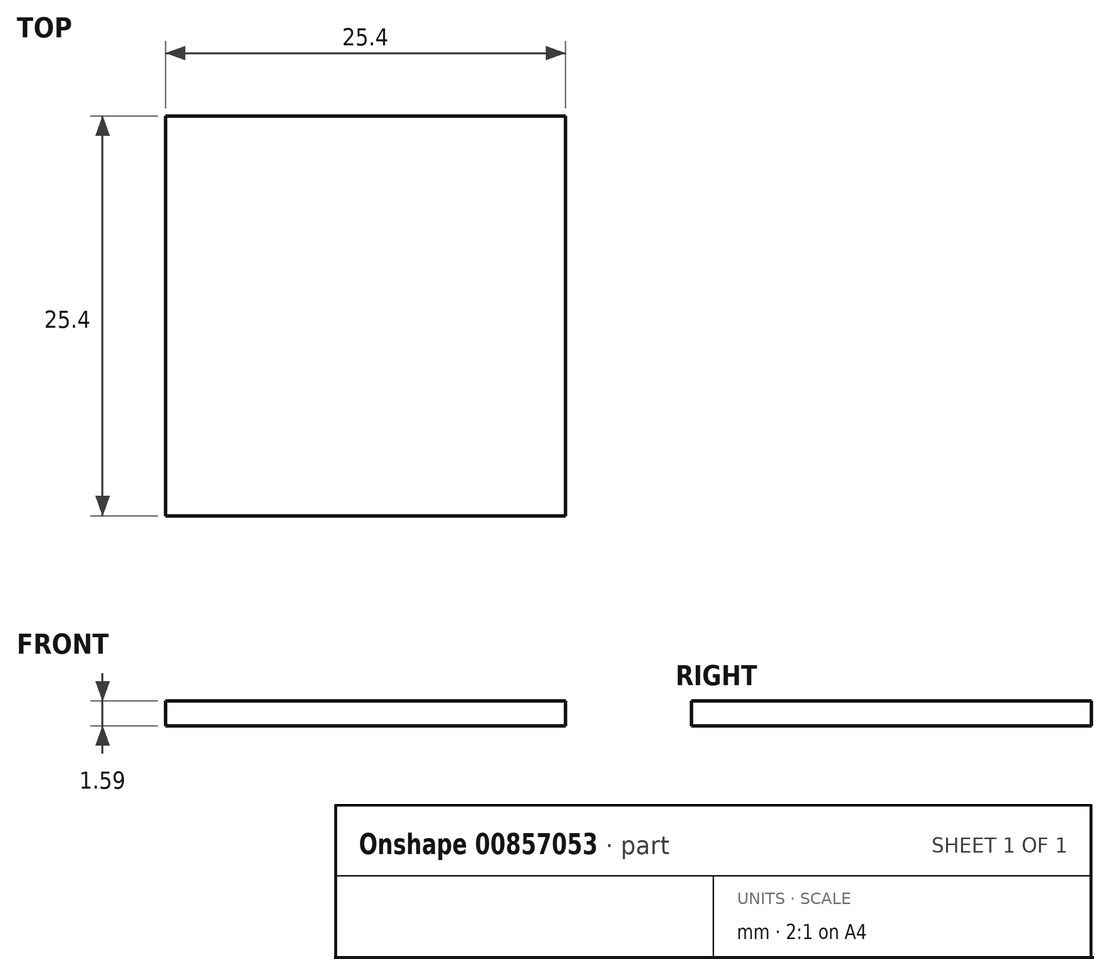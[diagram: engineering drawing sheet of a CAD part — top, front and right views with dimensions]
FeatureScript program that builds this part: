
annotation { "Feature Type Name" : "Feature", "Feature Type Description" : "" }
export const myFeature = defineFeature(function(context is Context, id is Id, definition is map)
    precondition{}
    {
        {
            var Q0;
            Q0=qCreatedBy(makeId("Top.planeOp"),FACE);
            var sketch = newSketch(context, id + "F0", { "sketchPlane" : qUnion([Q0])});
            skLineSegment(sketch, "E0.bottom", {"start": v(-12.7, 12.7) * mm, "end": v(12.7, 12.7) * mm});
            skLineSegment(sketch, "E0.top", {"start": v(-12.7, -12.7) * mm, "end": v(12.7, -12.7) * mm});
            skLineSegment(sketch, "E0.left", {"start": v(-12.7, 12.7) * mm, "end": v(-12.7, -12.7) * mm});
            skLineSegment(sketch, "E0.right", {"start": v(12.7, 12.7) * mm, "end": v(12.7, -12.7) * mm});
            skPoint(sketch, "E0.middle", {"position": v(0, 0) * mm});
            skSolve(sketch);
        }
        {
            var Q0;
            Q0=qSketchRegion(id+"F0",true);
            extrude(context, id + "F1", {"entities" : qUnion([Q0]), "depth" : 1.59 * mm, "offsetDistance" : 25.4 * mm});
        }
    });
